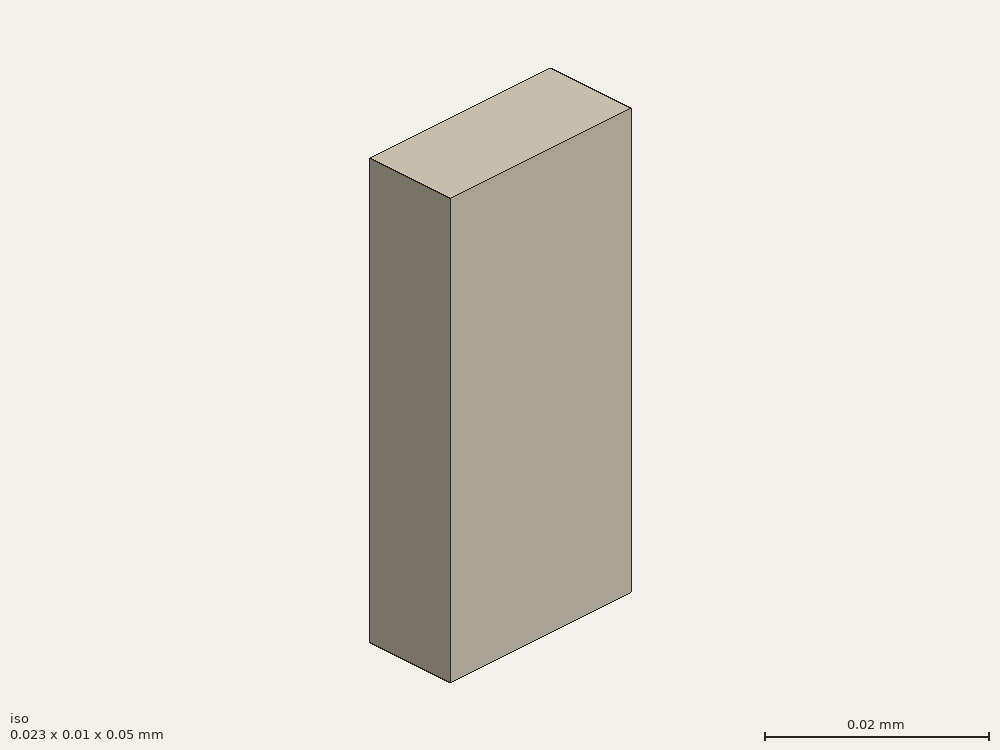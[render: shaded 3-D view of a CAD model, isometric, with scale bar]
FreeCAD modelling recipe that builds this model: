
FCSTD DOCUMENT  (FreeCAD 0.21R33694 (Git))
Label: shorted
License: All rights reserved
LicenseURL: http://en.wikipedia.org/wiki/All_rights_reserved
objects: Part::Part2DObjectPython×3, App::FeaturePython×2, Part::Extrusion×1, Part::FeaturePython×1
note: 5 computed .brp shape members not serialized (recipe doc carries the construction recipe); baked Part::Feature solids carry a one-line shape summary decoded from their .brp

FEATURE [Part::Part2DObjectPython] Rectangle  # Draft 2D object (typed FeaturePython)
  Area = 232.258
  ChamferSize = 0
  Columns = 1
  FilletRadius = 0
  Height = 10.16
  Length = 22.86
  MakeFace = true
  Placement = pos=(-11.43,-5.08,0) rot=(0,0,1;0rad)
  Rows = 1
FEATURE [Part::Extrusion] Extrude
  Base = -> Rectangle
  Dir = (0,0,1)
  DirMode = 2
  FaceMakerClass = Part::FaceMakerBullseye
  LengthFwd = 50
  LengthRev = 0
  Solid = false
  Symmetric = false
FEATURE [Part::FeaturePython] Clone  label="Extrude001"  # Draft clone (typed FeaturePython)
  AttacherType = Attacher::AttachEngine3D
  Fuse = false
  Objects = -> [Extrude]
  Scale = (0.001,0.001,0.001)
FEATURE [Part::Part2DObjectPython] Rectangle001  label="_Pport1"  # Draft 2D object (typed FeaturePython)
  Area = 0.000232258
  ChamferSize = 0
  Columns = 1
  FilletRadius = 0
  Height = 0.01016
  Length = 0.02286
  MakeFace = true
  Placement = pos=(-0.01143,-0.00508,0.05) rot=(0,0,1;0rad)
  Rows = 1
FEATURE [Part::Part2DObjectPython] Line  label="_Pv1"  # Draft 2D object (typed FeaturePython)
  Area = 0
  ChamferSize = 0
  Closed = false
  End = (-1.8e-15,0.00508,0.05)
  FilletRadius = 0
  Length = 0.01016
  MakeFace = true
  Placement = pos=(-0.011,-0.005,3e-15) rot=(0,0,1;0rad)
  Points = (2) [(0.011,-8e-05,0.05),(0.011,0.01008,0.05)]
  Start = (0,-0.00508,0.05)
  Subdivisions = 0
FEATURE [App::FeaturePython] Text  label="_S1(PV){port1}"  # WARN: FeaturePython — macro-defined, semantics opaque (R4)
  Placement = pos=(0.0413747,-0.017509,0) rot=(0,0,1;0rad)
  Text = .
FEATURE [App::FeaturePython] Text002  label="_L1(1,voltage){v1}"  # WARN: FeaturePython — macro-defined, semantics opaque (R4)
  Placement = pos=(0.0413747,-0.017509,0) rot=(0,0,1;0rad)
  Text = .
